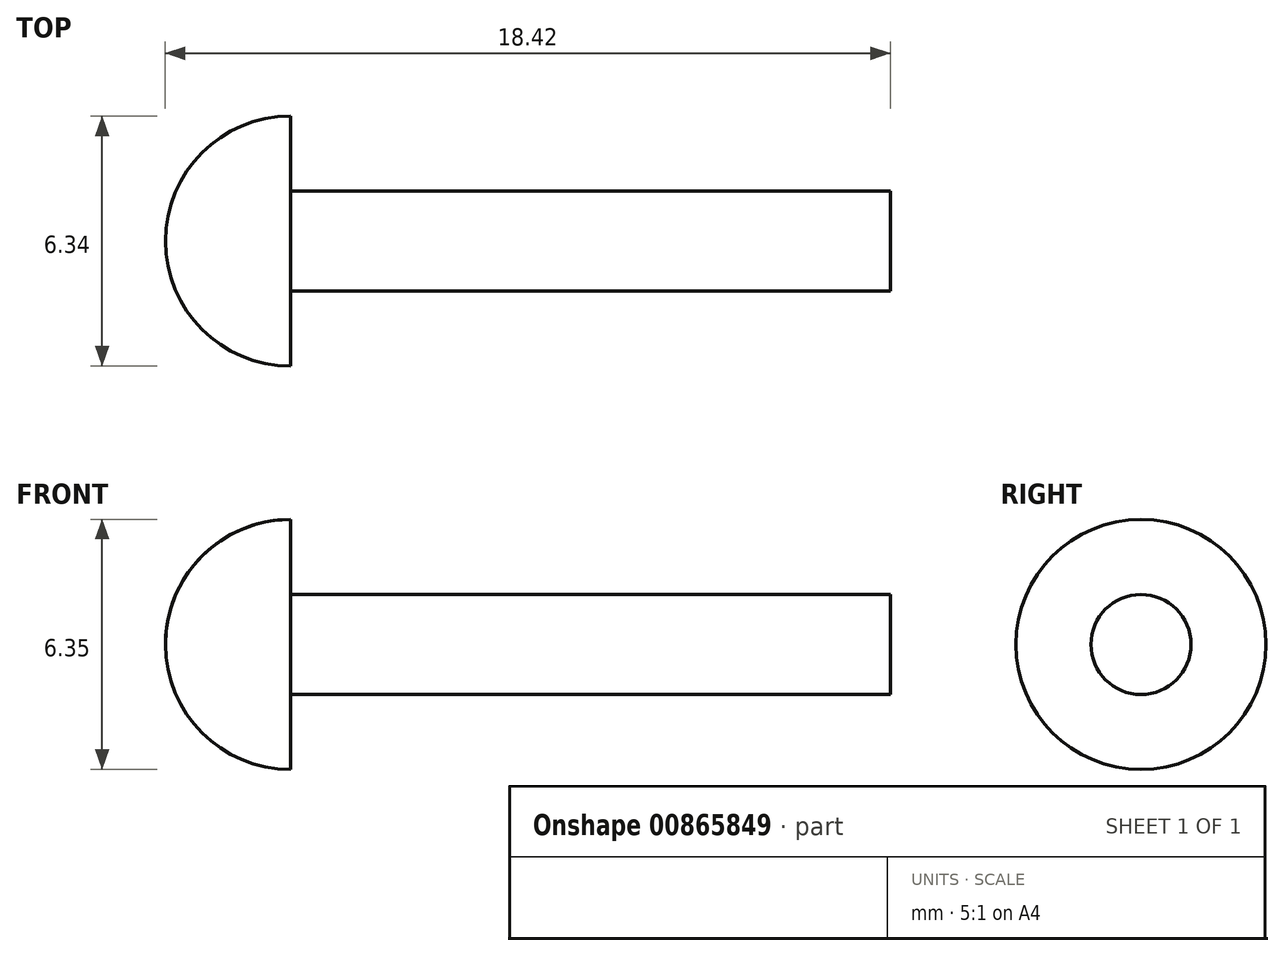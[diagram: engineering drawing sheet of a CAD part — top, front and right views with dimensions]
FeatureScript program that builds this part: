
annotation { "Feature Type Name" : "Feature", "Feature Type Description" : "" }
export const myFeature = defineFeature(function(context is Context, id is Id, definition is map)
    precondition{}
    {
        {
            var Q0;
            Q0=qCreatedBy(makeId("Right.planeOp"),FACE);
            var sketch = newSketch(context, id + "F0", { "sketchPlane" : qUnion([Q0])});
            skCircle(sketch, "E0", {"center": v(0, 0) * mm, "radius": 1.27 * mm});
            skSolve(sketch);
        }
        {
            var Q0;
            Q0 = qSketchRegion(id + "F0", true);
            extrude(context, id + "F1", {"entities" : qUnion([Q0]), "depth" : 15.24 * mm, "offsetDistance" : 25.4 * mm});
        }
        {
            var Q0;
            Q0=qCreatedBy(makeId("Front.planeOp"),FACE);
            var sketch = newSketch(context, id + "F2", { "sketchPlane" : qUnion([Q0])});
            skLineSegment(sketch, "E1", {"start": v(0, 0) * mm, "end": v(-3.18, 0) * mm});
            skLineSegment(sketch, "E2", {"start": v(0, 0) * mm, "end": v(0, 3.18) * mm});
            skArc(sketch, "E3", {"start": v(0, 3.18) * mm, "mid": v(-2.25, 2.25) * mm, "end": v(-3.18, 0) * mm});
            skSolve(sketch);
        }
        {
            var Q0;
            Q0 = qSketchRegion(id + "F2", true);
            var Q1;
            Q1=sQuery(id+"F2.wireOp",EDGE,"E1");
            revolve(context, id + "F3", {"operationType" : NewBodyOperationType.ADD, "surfaceOperationType" : NewSurfaceOperationType.NEW, "entities" : qUnion([Q0]), "axis" : qUnion([Q1]), "revolveType" : RevolveType.FULL});
        }
    });
